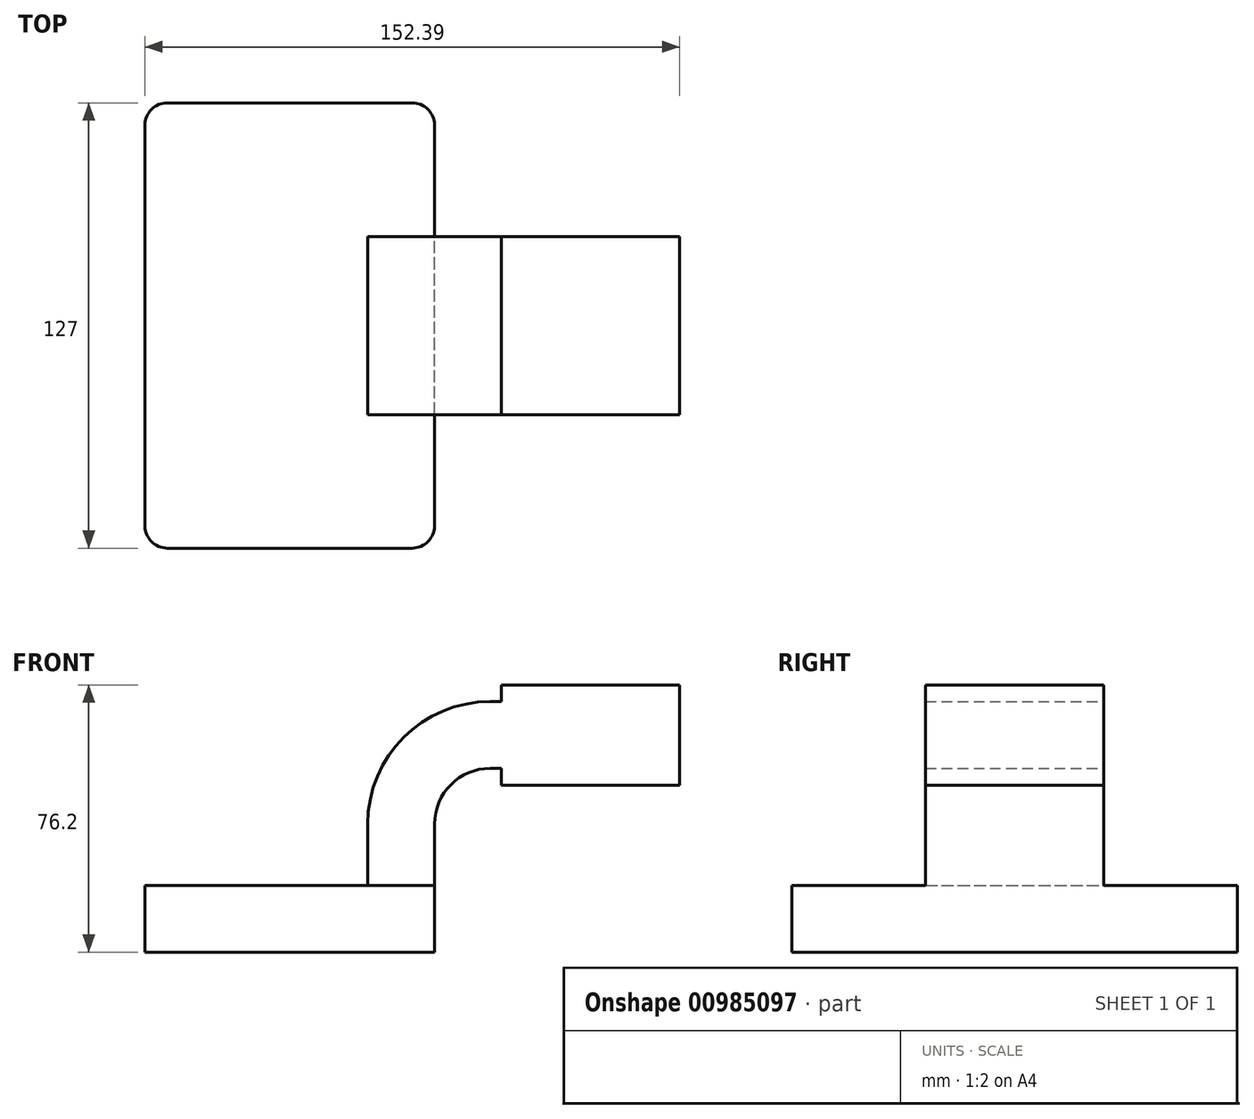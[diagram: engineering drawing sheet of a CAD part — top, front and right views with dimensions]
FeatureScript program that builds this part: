
annotation { "Feature Type Name" : "Feature", "Feature Type Description" : "" }
export const myFeature = defineFeature(function(context is Context, id is Id, definition is map)
    precondition{}
    {
        {
            var Q0;
            Q0=qCreatedBy(makeId("Front.planeOp"),FACE);
            var sketch = newSketch(context, id + "F0", { "sketchPlane" : qUnion([Q0])});
            skLineSegment(sketch, "E0.bottom", {"start": v(-41.28, -0.38) * mm, "end": v(41.28, -0.38) * mm});
            skLineSegment(sketch, "E0.top", {"start": v(-41.28, 18.67) * mm, "end": v(41.28, 18.67) * mm});
            skLineSegment(sketch, "E0.left", {"start": v(-41.28, -0.38) * mm, "end": v(-41.28, 18.67) * mm});
            skLineSegment(sketch, "E0.right", {"start": v(41.28, -0.38) * mm, "end": v(41.28, 18.67) * mm});
            skPoint(sketch, "E0.middle", {"position": v(0, 9.15) * mm});
            skLineSegment(sketch, "E1.bottom", {"start": v(60.33, 47.25) * mm, "end": v(111.12, 47.25) * mm});
            skLineSegment(sketch, "E1.top", {"start": v(60.32, 75.82) * mm, "end": v(111.12, 75.82) * mm});
            skLineSegment(sketch, "E1.left", {"start": v(60.33, 47.25) * mm, "end": v(60.33, 75.82) * mm});
            skLineSegment(sketch, "E1.right", {"start": v(111.13, 47.25) * mm, "end": v(111.13, 75.82) * mm});
            skPoint(sketch, "E1.middle", {"position": v(85.73, 61.54) * mm});
            skLineSegment(sketch, "E2", {"start": v(41.28, 18.67) * mm, "end": v(41.28, 36.15) * mm});
            skArc(sketch, "E3", {"start": v(41.28, 36.15) * mm, "mid": v(45.92, 47.37) * mm, "end": v(57.15, 52.02) * mm});
            skLineSegment(sketch, "E4", {"start": v(57.15, 52.02) * mm, "end": v(79.67, 52.02) * mm});
            skLineSegment(sketch, "E5.0", {"start": v(57.15, 71.07) * mm, "end": v(79.67, 71.07) * mm});
            skArc(sketch, "E5.1", {"start": v(22.23, 36.15) * mm, "mid": v(32.45, 60.85) * mm, "end": v(57.15, 71.07) * mm});
            skLineSegment(sketch, "E5.2", {"start": v(22.23, 18.67) * mm, "end": v(22.23, 36.15) * mm});
            skFitSpline(sketch, "E6", {"points": [v(-41.28, 18.67) * mm, v(57.15, 71.07) * mm], "startDerivative": vector(55.67, 109.66) * mm, "endDerivative": vector(116.68, -1.49) * mm});
            skLineSegment(sketch, "E7", {"start": v(79.67, 52.02) * mm, "end": v(79.67, 75.82) * mm});
            skLineSegment(sketch, "E8", {"start": v(79.67, 52.02) * mm, "end": v(79.67, 47.25) * mm});
            skSolve(sketch);
        }
        {
            var Q0;
            Q0=makeQuery(id+"F0.imprint","IMPRINT",FACE,{"disambiguationData":[TD([[makeQuery(id+"F0.imprint","IMPRINT",EDGE,{"derivedFrom":sQuery(id+"F0.wireOp",EDGE,"E0.bottom")}),1.0]])]});
            extrude(context, id + "F1", {"entities" : qUnion([Q0]), "endBound" : BoundingType.SYMMETRIC, "depth" : 127 * mm, "offsetDistance" : 25.4 * mm});
        }
        {
            var Q0;
            {var subQ1=sQuery(id+"F0.wireOp",EDGE,"E2");Q0=makeQuery(id+"F0.imprint","IMPRINT",FACE,{"disambiguationData":[TD([[makeQuery(id+"F0.imprint","IMPRINT",EDGE,{"derivedFrom":subQ1}),1.0]])]});}
            var Q1;
            {var subQ3=sQuery(id+"F0.wireOp",EDGE,"E1.right");Q1=makeQuery(id+"F0.imprint","IMPRINT",FACE,{"disambiguationData":[TD([[makeQuery(id+"F0.imprint","IMPRINT",EDGE,{"derivedFrom":subQ3}),1.0]])]});}
            var Q2;
            {var subQ0=sQuery(id+"F0.wireOp",EDGE,"E4");var subQ1=sQuery(id+"F0.wireOp",EDGE,"E1.left");var subQ2=makeQuery(id+"F0.imprint","INTERSECT",VERTEX,{"derivedFrom":[subQ1,subQ0]});Q2=makeQuery(id+"F0.imprint","IMPRINT",FACE,{"disambiguationData":[TD([[makeQuery(id+"F0.imprint","IMPRINT",EDGE,{"disambiguationData":[TD([[subQ2,-1.0]])],"derivedFrom":subQ1}),-1.0]])]});}
            var Q3;
            {var subQ0=sQuery(id+"F0.wireOp",EDGE,"E1.left");var subQ1=sQuery(id+"F0.wireOp",EDGE,"E1.top");var subQ2=makeQuery(id+"F0.imprint","INTERSECT",VERTEX,{"derivedFrom":[subQ1,subQ0]});Q3=makeQuery(id+"F0.imprint","IMPRINT",FACE,{"disambiguationData":[TD([[makeQuery(id+"F0.imprint","IMPRINT",EDGE,{"disambiguationData":[TD([[subQ2,-1.0]])],"derivedFrom":subQ1}),-1.0]])]});}
            var Q4;
            {var subQ3=sQuery(id+"F0.wireOp",EDGE,"E8");Q4=makeQuery(id+"F0.imprint","IMPRINT",FACE,{"disambiguationData":[TD([[makeQuery(id+"F0.imprint","IMPRINT",EDGE,{"derivedFrom":subQ3}),-1.0]])]});}
            extrude(context, id + "F2", {"entities" : qUnion([Q0, Q1, Q2, Q3, Q4]), "operationType" : NewBodyOperationType.ADD, "endBound" : BoundingType.SYMMETRIC, "depth" : 50.8 * mm, "offsetDistance" : 25.4 * mm});
        }
        {
            var Q0;
            Q0=makeQuery(id+"F0.imprint","IMPRINT",FACE,{"disambiguationData":[TD([[makeQuery(id+"F0.imprint","IMPRINT",EDGE,{"derivedFrom":sQuery(id+"F0.wireOp",EDGE,"E5.1")}),1.0]])]});
            extrude(context, id + "F3", {"entities" : qUnion([Q0]), "operationType" : NewBodyOperationType.ADD, "endBound" : BoundingType.SYMMETRIC, "depth" : 15.88 * mm, "offsetDistance" : 25.4 * mm});
        }
        {
            var Q0;
            Q0=makeQuery(id+"F1.opExtrude","CAP_EDGE",EDGE,{"disambiguationData":[OSD([sQuery(id+"F0.wireOp",EDGE,"E0.left")])],"isStart":true});
            var Q1;
            Q1=makeQuery(id+"F1.opExtrude","CAP_EDGE",EDGE,{"disambiguationData":[OSD([sQuery(id+"F0.wireOp",EDGE,"E0.left")])],"isStart":false});
            var Q2;
            Q2=makeQuery(id+"F1.opExtrude","CAP_EDGE",EDGE,{"disambiguationData":[OSD([sQuery(id+"F0.wireOp",EDGE,"E0.right")])],"isStart":true});
            var Q3;
            Q3=makeQuery(id+"F1.opExtrude","CAP_EDGE",EDGE,{"disambiguationData":[OSD([sQuery(id+"F0.wireOp",EDGE,"E0.right")])],"isStart":false});
            fillet(context, id + "F4", {"entities" : qUnion([Q0, Q1, Q2, Q3]), "radius" : 6.35 * mm, "tangentPropagation" : true, "allowEdgeOverflow" : false});
        }
    });
